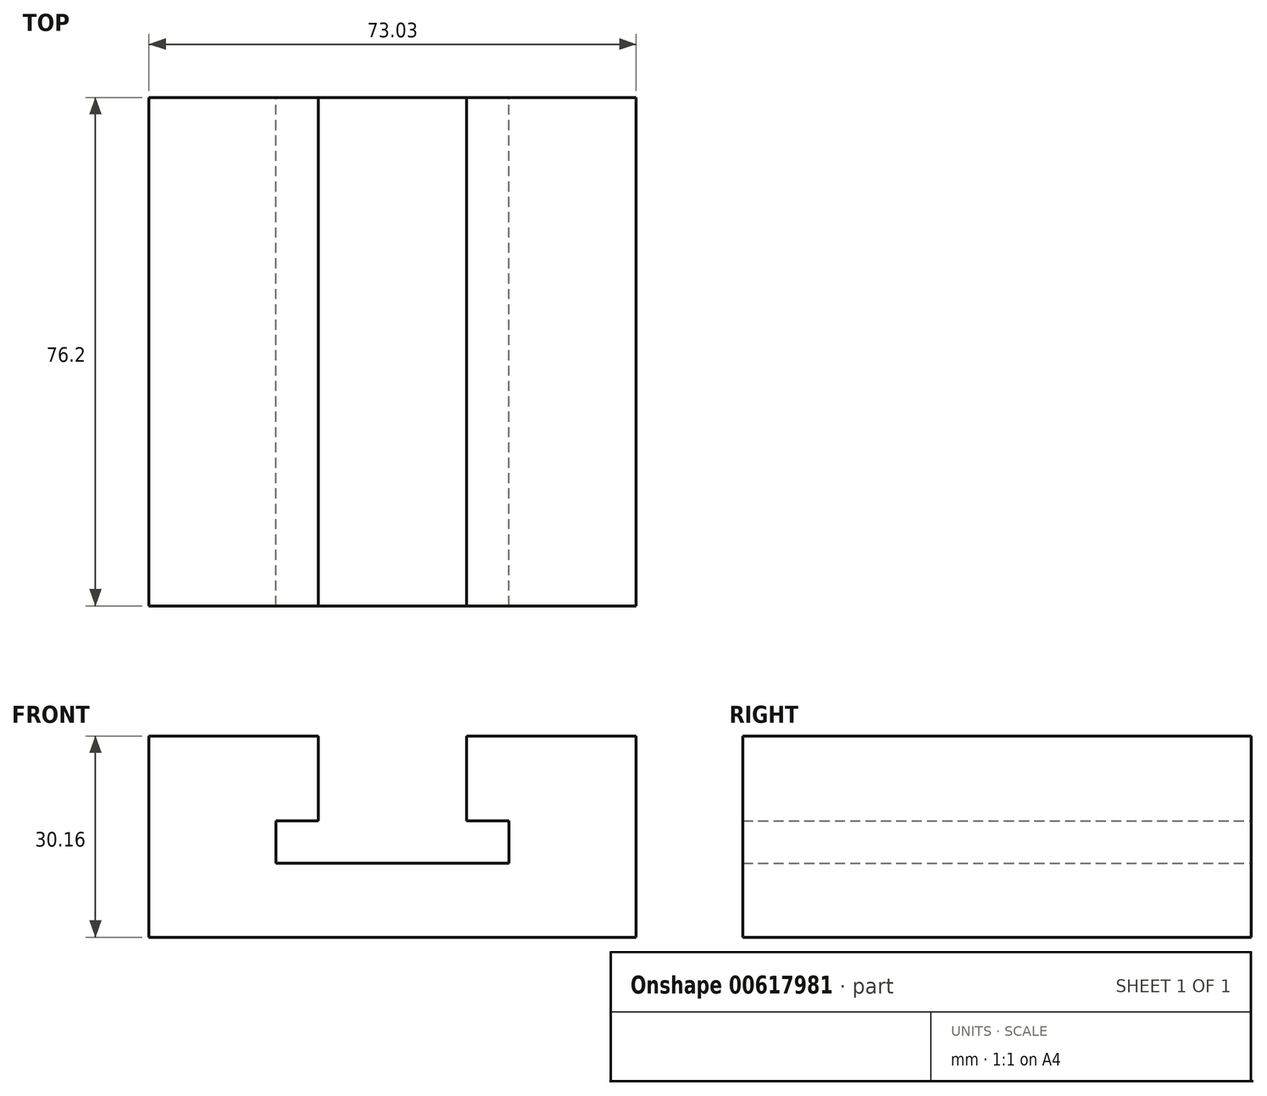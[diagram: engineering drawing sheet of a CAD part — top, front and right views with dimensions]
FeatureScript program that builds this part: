
annotation { "Feature Type Name" : "Feature", "Feature Type Description" : "" }
export const myFeature = defineFeature(function(context is Context, id is Id, definition is map)
    precondition{}
    {
        {
            var Q0;
            Q0=qCreatedBy(makeId("Front.planeOp"),FACE);
            var sketch = newSketch(context, id + "F0", { "sketchPlane" : qUnion([Q0])});
            skLineSegment(sketch, "E0", {"start": v(0, 0) * mm, "end": v(0, 30.16) * mm});
            skLineSegment(sketch, "E1", {"start": v(0, 30.16) * mm, "end": v(25.4, 30.16) * mm});
            skLineSegment(sketch, "E2", {"start": v(25.4, 30.16) * mm, "end": v(25.4, 17.46) * mm});
            skLineSegment(sketch, "E3", {"start": v(25.4, 17.46) * mm, "end": v(19.05, 17.46) * mm});
            skLineSegment(sketch, "E4", {"start": v(19.05, 17.46) * mm, "end": v(19.05, 11.11) * mm});
            skLineSegment(sketch, "E5", {"start": v(53.98, 11.11) * mm, "end": v(53.98, 17.46) * mm});
            skLineSegment(sketch, "E6", {"start": v(53.98, 17.46) * mm, "end": v(47.62, 17.46) * mm});
            skLineSegment(sketch, "E7", {"start": v(47.62, 17.46) * mm, "end": v(47.62, 30.16) * mm});
            skLineSegment(sketch, "E8", {"start": v(47.62, 30.16) * mm, "end": v(73.03, 30.16) * mm});
            skLineSegment(sketch, "E9", {"start": v(73.03, 30.16) * mm, "end": v(73.03, 0) * mm});
            skLineSegment(sketch, "E10", {"start": v(0, 0) * mm, "end": v(73.03, 0) * mm});
            skLineSegment(sketch, "E11", {"start": v(19.05, 11.11) * mm, "end": v(53.98, 11.11) * mm});
            skSolve(sketch);
        }
        {
            var Q0;
            Q0=makeQuery(id+"F0.imprint","IMPRINT",FACE,{"disambiguationData":[TD([[makeQuery(id+"F0.imprint","IMPRINT",EDGE,{"derivedFrom":sQuery(id+"F0.wireOp",EDGE,"E0")}),-1.0]])]});
            extrude(context, id + "F1", {"entities" : qUnion([Q0]), "depth" : 76.2 * mm, "offsetDistance" : 25.4 * mm});
        }
    });
